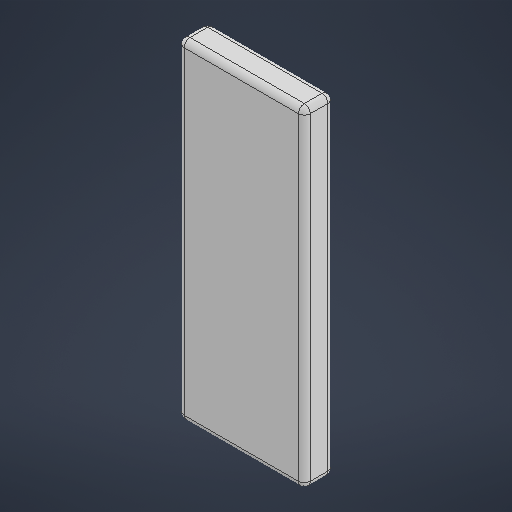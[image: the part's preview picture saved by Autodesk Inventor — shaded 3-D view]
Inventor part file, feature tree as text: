
AUTODESK INVENTOR PART (.ipt)
format: ipt  version: 2025 (Build 290162000, 162)  size: 196,608 bytes
history: native  units: mm
features: extrude x1, fillet x1, sketch x1
ambient origin geometry x8: Origin, YZ Plane, XZ Plane, XY Plane, X Axis, Y Axis, Z Axis, Center Point
bodies: 实体1 (feature_tree)
feature tree (3):
  extrude  "拉伸1"  Depth=21.4mm
  fillet  "圆角1"  Radius=5.0mm
  sketch  "草图1"  dims[d0=56.0mm d1=21.4mm d2=5.0mm d3=0.0mm d4=1.0mm]
